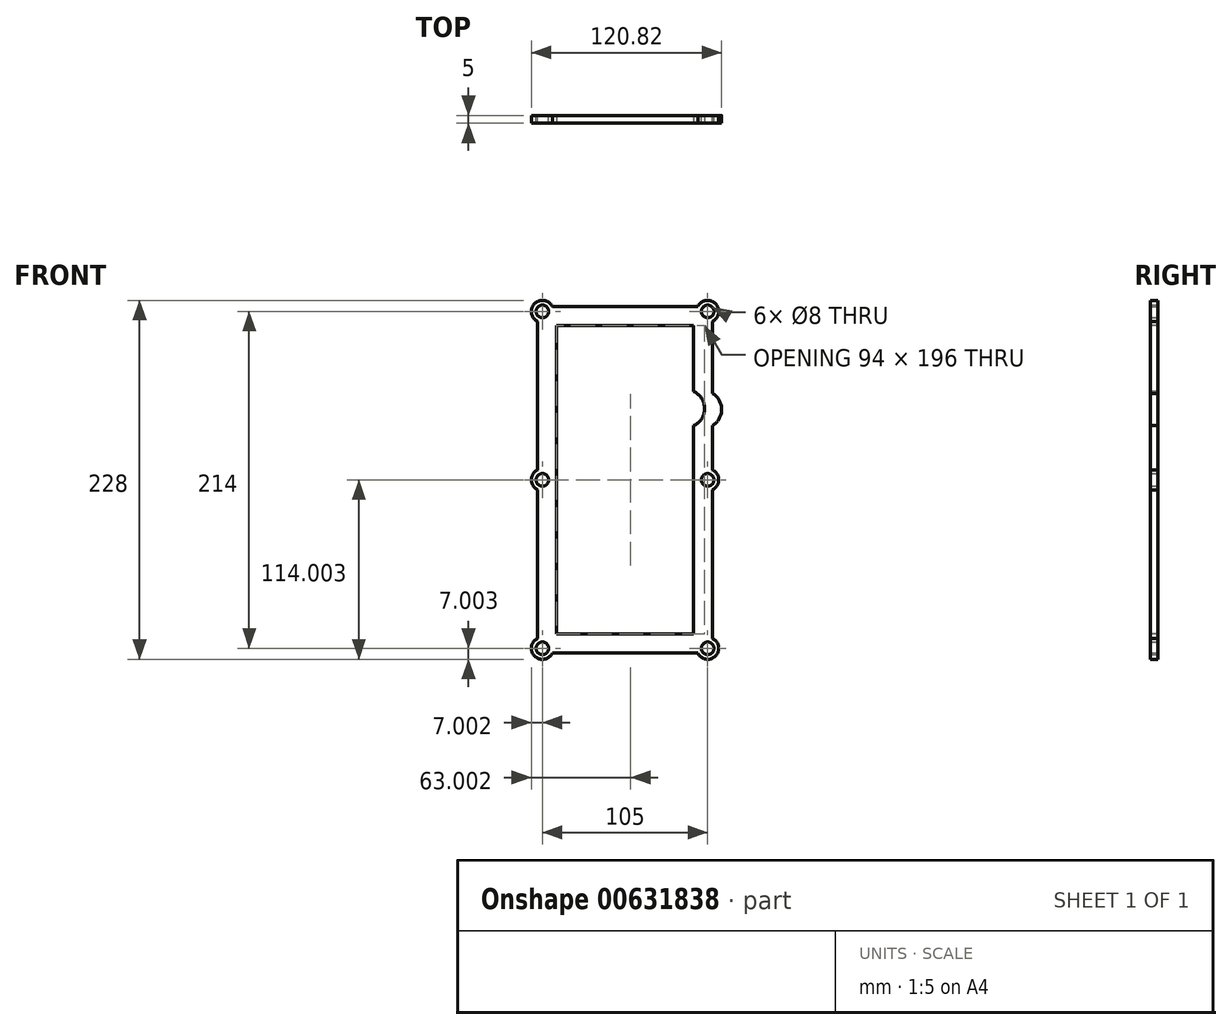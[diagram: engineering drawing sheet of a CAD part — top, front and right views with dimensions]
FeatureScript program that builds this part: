
annotation { "Feature Type Name" : "Feature", "Feature Type Description" : "" }
export const myFeature = defineFeature(function(context is Context, id is Id, definition is map)
    precondition{}
    {
        {
            var Q0;
            Q0=qCreatedBy(makeId("Front.planeOp"),FACE);
            var sketch = newSketch(context, id + "F0", { "sketchPlane" : qUnion([Q0])});
            skLineSegment(sketch, "E0.bottom", {"start": v(-55.4, 94.47) * mm, "end": v(49.6, 94.47) * mm, "construction": true});
            skLineSegment(sketch, "E0.top", {"start": v(-55.4, -119.53) * mm, "end": v(49.6, -119.53) * mm, "construction": true});
            skLineSegment(sketch, "E0.left", {"start": v(-55.4, 94.47) * mm, "end": v(-55.4, -119.53) * mm, "construction": true});
            skLineSegment(sketch, "E0.right", {"start": v(49.6, 94.47) * mm, "end": v(49.6, -119.53) * mm, "construction": true});
            skCircle(sketch, "E1", {"center": v(-55.4, 94.47) * mm, "radius": 4 * mm});
            skCircle(sketch, "E2", {"center": v(49.6, 94.47) * mm, "radius": 4 * mm});
            skCircle(sketch, "E3", {"center": v(49.6, -12.53) * mm, "radius": 4 * mm});
            skCircle(sketch, "E4", {"center": v(49.6, -119.53) * mm, "radius": 4 * mm});
            skCircle(sketch, "E5", {"center": v(-55.4, -119.53) * mm, "radius": 4 * mm});
            skCircle(sketch, "E6", {"center": v(-55.4, -12.53) * mm, "radius": 4 * mm});
            skPoint(sketch, "E7.middle", {"position": v(0, -10.99) * mm});
            skArc(sketch, "E8", {"start": v(-58.4, -113.2) * mm, "mid": v(-60.36, -124.48) * mm, "end": v(-49.08, -122.53) * mm});
            skArc(sketch, "E9", {"start": v(-49.08, 97.47) * mm, "mid": v(-60.36, 99.42) * mm, "end": v(-58.4, 88.15) * mm});
            skArc(sketch, "E10", {"start": v(52.6, 88.15) * mm, "mid": v(54.54, 99.42) * mm, "end": v(43.27, 97.47) * mm});
            skArc(sketch, "E11", {"start": v(52.6, -18.85) * mm, "mid": v(56.6, -12.53) * mm, "end": v(52.6, -6.2) * mm});
            skArc(sketch, "E12", {"start": v(-58.4, -6.2) * mm, "mid": v(-62.4, -12.53) * mm, "end": v(-58.4, -18.85) * mm});
            skArc(sketch, "E13", {"start": v(43.27, -122.53) * mm, "mid": v(54.54, -124.48) * mm, "end": v(52.6, -113.2) * mm});
            skLineSegment(sketch, "E14", {"start": v(-49.08, 97.47) * mm, "end": v(43.27, 97.47) * mm});
            skLineSegment(sketch, "E15", {"start": v(-58.4, 88.15) * mm, "end": v(-58.4, -6.2) * mm});
            skLineSegment(sketch, "E16", {"start": v(52.6, 88.15) * mm, "end": v(52.6, 42.43) * mm});
            skLineSegment(sketch, "E17", {"start": v(52.6, -18.85) * mm, "end": v(52.6, -113.2) * mm});
            skLineSegment(sketch, "E18", {"start": v(-58.4, -18.85) * mm, "end": v(-58.4, -113.2) * mm});
            skLineSegment(sketch, "E19", {"start": v(-49.08, -122.53) * mm, "end": v(43.27, -122.53) * mm});
            skLineSegment(sketch, "E20", {"start": v(30.5, 31.47) * mm, "end": v(49.6, 31.47) * mm, "construction": true});
            skArc(sketch, "E21", {"start": v(52.6, 21.9) * mm, "mid": v(58.4, 32.16) * mm, "end": v(52.6, 42.43) * mm});
            skLineSegment(sketch, "E22.trimOffspring", {"start": v(52.6, 21.9) * mm, "end": v(52.6, -6.2) * mm});
            skSolve(sketch);
        }
        {
            var Q0;
            Q0=qSketchRegion(id+"F0",true);
            var Q1;
            Q1 = qSketchRegion(id + "F2", true);
            extrude(context, id + "F1", {"entities" : qUnion([Q0, Q1]), "endBound" : BoundingType.SYMMETRIC, "depth" : 5 * mm, "offsetDistance" : 25 * mm});
        }
        {
            var Q0;
            Q0=qCreatedBy(makeId("Front.planeOp"),FACE);
            var sketch = newSketch(context, id + "F2", { "sketchPlane" : qUnion([Q0])});
            skLineSegment(sketch, "E23.bottom", {"start": v(-46.4, 85.47) * mm, "end": v(40.6, 85.47) * mm});
            skLineSegment(sketch, "E23.top", {"start": v(-46.4, -110.53) * mm, "end": v(40.6, -110.53) * mm});
            skLineSegment(sketch, "E23.left", {"start": v(-46.4, 85.47) * mm, "end": v(-46.4, -110.53) * mm});
            skLineSegment(sketch, "E23.right", {"start": v(40.6, 85.47) * mm, "end": v(40.6, 43.65) * mm});
            skLineSegment(sketch, "E24", {"start": v(56.62, 32.74) * mm, "end": v(35.6, 32.74) * mm, "construction": true});
            skArc(sketch, "E25", {"start": v(40.6, 21.83) * mm, "mid": v(47.6, 32.74) * mm, "end": v(40.6, 43.65) * mm});
            skLineSegment(sketch, "E26.trimOffspring", {"start": v(40.6, 21.83) * mm, "end": v(40.6, -110.53) * mm});
            skSolve(sketch);
        }
        {
            var Q0;
            Q0=qSketchRegion(id+"F2",true);
            extrude(context, id + "F3", {"entities" : qUnion([Q0]), "operationType" : NewBodyOperationType.REMOVE, "endBound" : BoundingType.SYMMETRIC, "oppositeDirection" : true, "depth" : 10 * mm, "offsetDistance" : 25 * mm});
        }
    });
